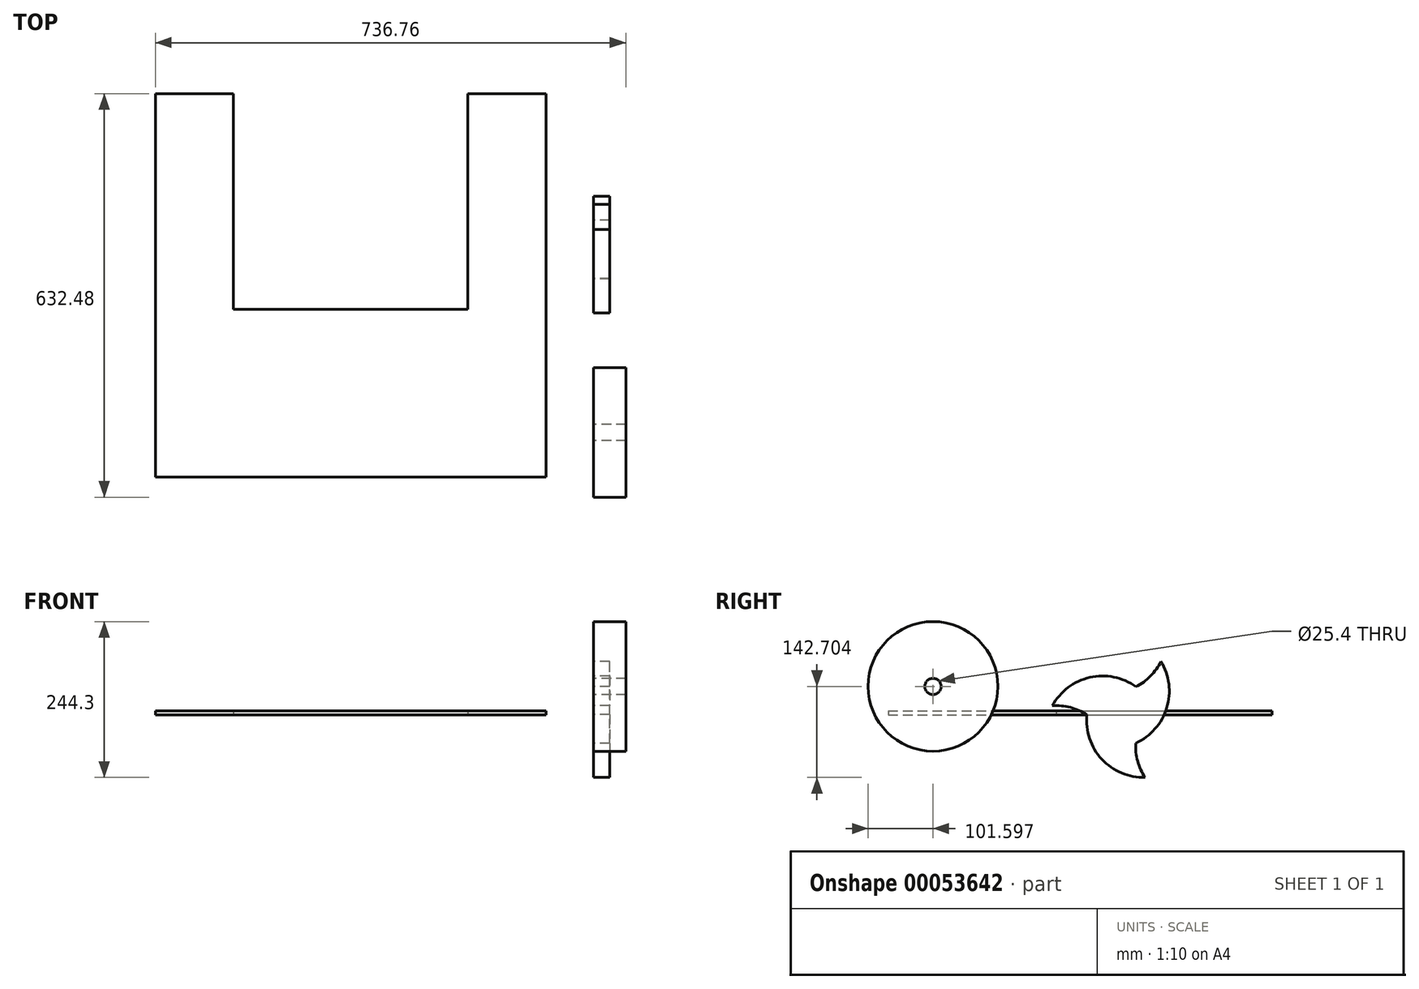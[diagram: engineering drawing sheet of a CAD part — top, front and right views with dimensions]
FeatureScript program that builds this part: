
annotation { "Feature Type Name" : "Feature", "Feature Type Description" : "" }
export const myFeature = defineFeature(function(context is Context, id is Id, definition is map)
    precondition{}
    {
        {
            var Q0;
            Q0=qCreatedBy(makeId("Right.planeOp"),FACE);
            var sketch = newSketch(context, id + "F0", { "sketchPlane" : qUnion([Q0])});
            skCircle(sketch, "E0.0", {"center": v(0, 0) * mm, "radius": 9.97 * mm});
            skCircle(sketch, "E1", {"center": v(0, 0) * mm, "radius": 3.18 * mm});
            skSolve(sketch);
        }
        {
            var Q0;
            Q0 = qSketchRegion(id + "F0", true);
            extrude(context, id + "F1", {"entities" : qUnion([Q0]), "depth" : 12.7 * mm});
        }
        {
            var Q0;
            Q0=qCreatedBy(makeId("Front.planeOp"),FACE);
            var sketch = newSketch(context, id + "F2", { "sketchPlane" : qUnion([Q0])});
            skLineSegment(sketch, "E2.left", {"start": v(0, 15.41) * mm, "end": v(0, 15.41) * mm});
            skLineSegment(sketch, "E2.right", {"start": v(12.7, 3.14) * mm, "end": v(12.7, 15.41) * mm});
            skLineSegment(sketch, "E3", {"start": v(0, 15.41) * mm, "end": v(3.5, 15.41) * mm});
            skLineSegment(sketch, "E4", {"start": v(12.7, 15.41) * mm, "end": v(9.4, 15.41) * mm});
            skLineSegment(sketch, "E5", {"start": v(9.4, 15.41) * mm, "end": v(9.4, 5.55) * mm});
            skLineSegment(sketch, "E6", {"start": v(9.4, 5.55) * mm, "end": v(3.5, 5.55) * mm});
            skLineSegment(sketch, "E7", {"start": v(3.5, 5.55) * mm, "end": v(3.5, 15.41) * mm});
            skLineSegment(sketch, "E8", {"start": v(0, 15.41) * mm, "end": v(0, 3.14) * mm});
            skLineSegment(sketch, "E9", {"start": v(0, 3.14) * mm, "end": v(12.7, 3.14) * mm});
            skLineSegment(sketch, "E10", {"start": v(0, 0) * mm, "end": v(12.7, 0) * mm, "construction": true});
            skSolve(sketch);
        }
        {
            var Q0;
            Q0 = qSketchRegion(id + "F2", true);
            var Q1;
            Q1=sQuery(id+"F2.wireOp",EDGE,"E10");
            revolve(context, id + "F3", {"operationType" : NewBodyOperationType.ADD, "entities" : qUnion([Q0]), "axis" : qUnion([Q1]), "revolveType" : RevolveType.ONE_DIRECTION, "angle" : 55 * degree});
        }
        {
            var Q0;
            Q0=makeQuery(id+"F3.boolean.opBoolean","MERGE",FACE,{"derivedFrom":[makeQuery(id+"F1.opExtrude","CAP_FACE",FACE,{"disambiguationData":[OSD([sQuery(id+"F0.wireOp",EDGE,"E0.0"),sQuery(id+"F0.wireOp",EDGE,"E1")])],"isStart":true}),makeQuery(id+"F3.opRevolve","SWEPT_FACE",FACE,{"disambiguationData":[OSD([sQuery(id+"F2.wireOp",EDGE,"E8")])]})]});
            var sketch = newSketch(context, id + "F4", { "sketchPlane" : qUnion([Q0])});
            skArc(sketch, "E11", {"start": v(8.17, 5.72) * mm, "mid": v(6.2, 11.93) * mm, "end": v(0, 9.97) * mm});
            skSolve(sketch);
        }
        {
            var Q0;
            {var subQ1=sQuery(id+"F2.wireOp",EDGE,"E3");var subQ4=sQuery(id+"F2.wireOp",EDGE,"E8");var subQ18=makeQuery(id+"F3.opRevolve","SWEPT_EDGE",EDGE,{"disambiguationData":[OSD([subQ1,subQ4])]});Q0=makeQuery(id+"F4.imprint","IMPRINT",FACE,{"disambiguationData":[TD([[makeQuery(id+"F4.imprint","IMPRINT",EDGE,{"derivedFrom":subQ18}),1.0]])]});}
            extrude(context, id + "F5", {"entities" : qUnion([Q0]), "operationType" : NewBodyOperationType.REMOVE, "oppositeDirection" : true, "depth" : 25.4 * mm});
        }
        {
            var Q0;
            Q0=qCreatedBy(makeId("Front.planeOp"),FACE);
            var sketch = newSketch(context, id + "F6", { "sketchPlane" : qUnion([Q0])});
            skLineSegment(sketch, "E12", {"start": v(0, -3.24) * mm, "end": v(0, -14.6) * mm});
            skLineSegment(sketch, "E13", {"start": v(0, -14.6) * mm, "end": v(12.7, -14.6) * mm});
            skLineSegment(sketch, "E14", {"start": v(12.7, -14.6) * mm, "end": v(12.7, -3.24) * mm});
            skLineSegment(sketch, "E15", {"start": v(12.7, -3.24) * mm, "end": v(0, -3.24) * mm});
            skLineSegment(sketch, "E16", {"start": v(0, 0) * mm, "end": v(12.7, 0) * mm, "construction": true});
            skSolve(sketch);
        }
        {
            var Q0;
            Q0 = qSketchRegion(id + "F6", true);
            var Q1;
            Q1=sQuery(id+"F6.wireOp",EDGE,"E16");
            revolve(context, id + "F7", {"operationType" : NewBodyOperationType.ADD, "entities" : qUnion([Q0]), "axis" : qUnion([Q1]), "revolveType" : RevolveType.TWO_DIRECTIONS, "angle" : 15 * degree, "angleBack" : 340 * degree});
        }
        {
            var Q0;
            Q0=makeQuery(id+"F1.opExtrude","SWEPT_BODY",BODY,{"disambiguationData":[OSD([sQuery(id+"F0.wireOp",EDGE,"E0.0"),sQuery(id+"F0.wireOp",EDGE,"E1")])]});
            deleteBodies(context, id + "F8", {"entities" : qUnion([Q0])});
        }
        {
            var Q0;
            Q0=qCreatedBy(makeId("Right.planeOp"),FACE);
            var sketch = newSketch(context, id + "F9", { "sketchPlane" : qUnion([Q0])});
            skCircle(sketch, "E17", {"center": v(-119.55, 44.54) * mm, "radius": 101.6 * mm});
            skCircle(sketch, "E18", {"center": v(-119.55, 44.54) * mm, "radius": 12.7 * mm});
            skSolve(sketch);
        }
        {
            var Q0;
            Q0 = qSketchRegion(id + "F9", true);
            extrude(context, id + "F10", {"entities" : qUnion([Q0]), "depth" : 50.8 * mm});
        }
        {
            var Q0;
            Q0=qCreatedBy(makeId("Right.planeOp"),FACE);
            var sketch = newSketch(context, id + "F11", { "sketchPlane" : qUnion([Q0])});
            skArc(sketch, "E19", {"start": v(201.73, 41.54) * mm, "mid": v(128.24, 59.12) * mm, "end": v(67.41, 14.29) * mm});
            skArc(sketch, "E20", {"start": v(121.68, 0) * mm, "mid": v(95.72, 11.62) * mm, "end": v(67.41, 14.29) * mm});
            skArc(sketch, "E21.1.0", {"start": v(197.88, -44) * mm, "mid": v(200.8, -72.28) * mm, "end": v(212.64, -98.14) * mm});
            skArc(sketch, "E21.1.1", {"start": v(121.89, 4.56) * mm, "mid": v(143.4, -67.87) * mm, "end": v(212.64, -98.14) * mm});
            skArc(sketch, "E21.2.0", {"start": v(197.88, 44) * mm, "mid": v(220.92, 60.66) * mm, "end": v(237.39, 83.85) * mm});
            skArc(sketch, "E21.2.1", {"start": v(193.83, -46.1) * mm, "mid": v(245.8, 8.75) * mm, "end": v(237.39, 83.85) * mm});
            skPoint(sketch, "E21.center", {"position": v(172.48, 0) * mm});
            skSolve(sketch);
        }
        {
            var Q0;
            Q0 = qSketchRegion(id + "F11", true);
            extrude(context, id + "F12", {"entities" : qUnion([Q0]), "depth" : 25.4 * mm});
        }
        {
            var Q0;
            Q0=qCreatedBy(makeId("Top.planeOp"),FACE);
            var sketch = newSketch(context, id + "F13", { "sketchPlane" : qUnion([Q0])});
            skLineSegment(sketch, "E22.bottom", {"start": v(-74.45, -189.5) * mm, "end": v(-685.96, -189.5) * mm});
            skLineSegment(sketch, "E22.top", {"start": v(-74.45, 73.5) * mm, "end": v(-685.96, 73.5) * mm});
            skLineSegment(sketch, "E22.left", {"start": v(-74.45, -189.5) * mm, "end": v(-74.45, 73.5) * mm});
            skLineSegment(sketch, "E22.right", {"start": v(-685.96, -189.5) * mm, "end": v(-685.96, 73.5) * mm});
            skLineSegment(sketch, "E23.bottom", {"start": v(-685.96, 73.5) * mm, "end": v(-563.74, 73.5) * mm});
            skLineSegment(sketch, "E23.top", {"start": v(-685.96, 411.33) * mm, "end": v(-563.74, 411.33) * mm});
            skLineSegment(sketch, "E23.left", {"start": v(-685.96, 73.5) * mm, "end": v(-685.96, 411.33) * mm});
            skLineSegment(sketch, "E23.right", {"start": v(-563.74, 73.5) * mm, "end": v(-563.74, 411.33) * mm});
            skLineSegment(sketch, "E24", {"start": v(-380.2, -133.63) * mm, "end": v(-380.2, -23.5) * mm});
            skPoint(sketch, "E24.startSnap0", {"position": v(-380.2, 73.5) * mm});
            skLineSegment(sketch, "E25.MirrorCS", {"start": v(-74.45, 411.33) * mm, "end": v(-196.67, 411.33) * mm});
            skLineSegment(sketch, "E26.MirrorCS", {"start": v(-74.45, 73.5) * mm, "end": v(-196.67, 73.5) * mm});
            skLineSegment(sketch, "E27.MirrorCS", {"start": v(-74.45, 73.5) * mm, "end": v(-74.45, 411.33) * mm});
            skLineSegment(sketch, "E28.MirrorCS", {"start": v(-196.67, 73.5) * mm, "end": v(-196.67, 411.33) * mm});
            skSolve(sketch);
        }
        {
            var Q0;
            Q0 = qSketchRegion(id + "F13", true);
            extrude(context, id + "F14", {"entities" : qUnion([Q0]), "depth" : 6.35 * mm});
        }
    });
